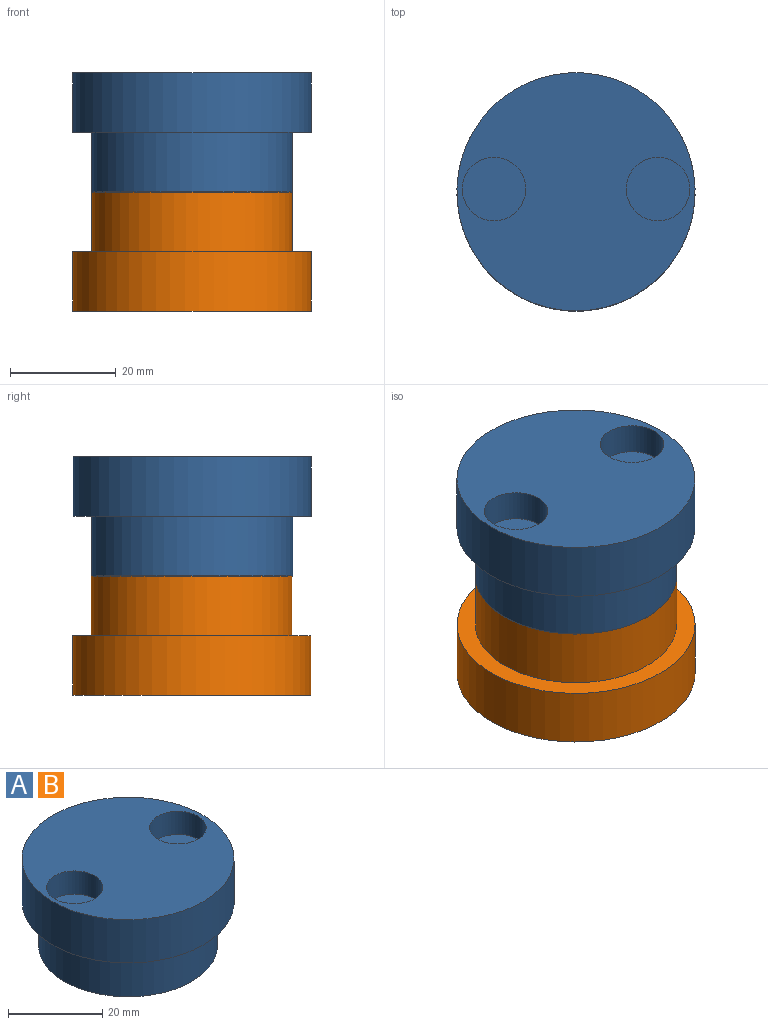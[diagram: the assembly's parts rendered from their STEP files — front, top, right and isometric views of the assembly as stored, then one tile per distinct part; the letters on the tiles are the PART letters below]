
ASSEMBLY  parts=2 mates=1
PART A: 11 faces, bbox 45x45x22.5 mm
  f0: plane 45x45mm, normal (0,0,1), area 1364.2mm2, adj f1,f7,f9
  f1: cylinder r=22.5mm len=45mm, axis (0,0,1), area 1590.4mm2, adj f0,f2
  f2: plane 45x45mm, normal (0,0,-1), area 456.3mm2, adj f1,f3
  f3: cylinder r=19mm len=38mm, axis (0,0,1), area 1343mm2, adj f2,f4
  f4: plane 38x38mm, normal (0,0,-1), area 1021mm2, adj f3,f5
  f5: cylinder r=6mm len=12mm, axis (0,0,-1), area 226.2mm2, adj f4,f6
  f6: plane 12x12mm, normal (0,0,-1), area 113.1mm2, adj f5
  f7: cylinder r=6mm len=12mm, axis (0,0,1), area 226.2mm2, adj f0,f8
  f8: plane 12x12mm, normal (0,0,1), area 113.1mm2, adj f7
  f9: cylinder r=6mm len=12mm, axis (0,0,1), area 226.2mm2, adj f0,f10
  f10: plane 12x12mm, normal (0,0,1), area 113.1mm2, adj f9
PART B: same geometry as A
PLACE A t=(-31.34,11.64,9.58)mm
PLACE B rot(axis=(1,0,0),180deg) t=(-31.34,-21.14,-97.14)mm
MATE fastened B.f5 <-> A.f5  axis (0,0,1) through (-31.34,-4.75,-43.78)mm
